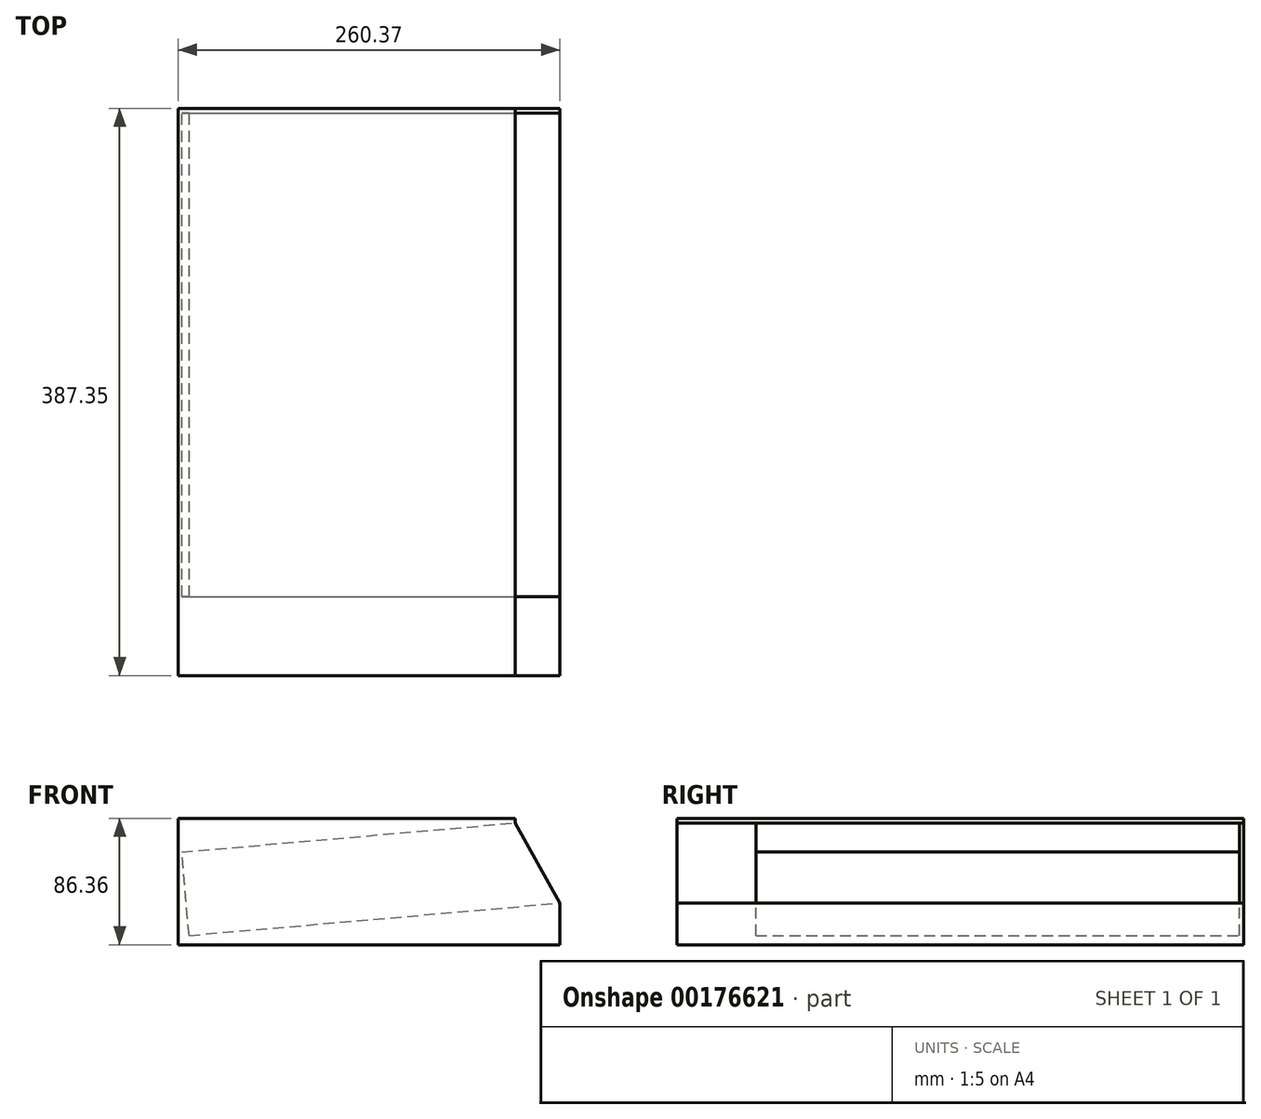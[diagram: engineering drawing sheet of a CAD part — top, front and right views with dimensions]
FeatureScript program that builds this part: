
annotation { "Feature Type Name" : "Feature", "Feature Type Description" : "" }
export const myFeature = defineFeature(function(context is Context, id is Id, definition is map)
    precondition{}
    {
        {
            var Q0;
            Q0=qCreatedBy(makeId("Front.planeOp"),FACE);
            var sketch = newSketch(context, id + "F0", { "sketchPlane" : qUnion([Q0])});
            skLineSegment(sketch, "E0", {"start": v(-29.65, 0) * mm, "end": v(230.72, 0) * mm});
            skLineSegment(sketch, "E1", {"start": v(-29.65, 0) * mm, "end": v(-29.65, 86.36) * mm});
            skLineSegment(sketch, "E2", {"start": v(-22.32, 6.35) * mm, "end": v(-27.3, 63.28) * mm});
            skLineSegment(sketch, "E3", {"start": v(-22.32, 6.35) * mm, "end": v(230.72, 28.49) * mm});
            skLineSegment(sketch, "E4", {"start": v(-27.3, 63.28) * mm, "end": v(200.43, 83.2) * mm});
            skLineSegment(sketch, "E5", {"start": v(-29.65, 86.36) * mm, "end": v(200.43, 86.36) * mm});
            skLineSegment(sketch, "E6", {"start": v(230.72, 28.49) * mm, "end": v(230.72, 0) * mm});
            skLineSegment(sketch, "E7", {"start": v(200.43, 83.2) * mm, "end": v(200.43, 86.36) * mm});
            skLineSegment(sketch, "E8", {"start": v(200.43, 83.2) * mm, "end": v(230.72, 28.49) * mm});
            skSolve(sketch);
        }
        {
            var Q0;
            Q0=makeQuery(id+"F0.imprint","IMPRINT",FACE,{"disambiguationData":[TD([[makeQuery(id+"F0.imprint","IMPRINT",EDGE,{"derivedFrom":sQuery(id+"F0.wireOp",EDGE,"E0")}),1.0]])]});
            var Q1;
            Q1=makeQuery(id+"F0.imprint","IMPRINT",FACE,{"disambiguationData":[TD([[makeQuery(id+"F0.imprint","IMPRINT",EDGE,{"derivedFrom":sQuery(id+"F0.wireOp",EDGE,"E2")}),-1.0]])]});
            extrude(context, id + "F1", {"entities" : qUnion([Q0, Q1]), "oppositeDirection" : true, "depth" : 3.17 * mm});
        }
        {
            var Q0;
            Q0=makeQuery(id+"F0.imprint","IMPRINT",FACE,{"disambiguationData":[TD([[makeQuery(id+"F0.imprint","IMPRINT",EDGE,{"derivedFrom":sQuery(id+"F0.wireOp",EDGE,"E0")}),1.0]])]});
            extrude(context, id + "F2", {"entities" : qUnion([Q0]), "operationType" : NewBodyOperationType.ADD, "depth" : 330.2 * mm});
        }
        {
            var Q0;
            Q0=makeQuery(id+"F2.opExtrude","CAP_FACE",FACE,{"disambiguationData":[OSD([sQuery(id+"F0.wireOp",EDGE,"E0"),sQuery(id+"F0.wireOp",EDGE,"E1"),sQuery(id+"F0.wireOp",EDGE,"E2"),sQuery(id+"F0.wireOp",EDGE,"E3"),sQuery(id+"F0.wireOp",EDGE,"E4"),sQuery(id+"F0.wireOp",EDGE,"E5"),sQuery(id+"F0.wireOp",EDGE,"E6"),sQuery(id+"F0.wireOp",EDGE,"E7")])],"isStart":false});
            var sketch = newSketch(context, id + "F3", { "sketchPlane" : qUnion([Q0])});
            skLineSegment(sketch, "E9", {"start": v(200.43, 83.2) * mm, "end": v(230.72, 28.49) * mm});
            skLineSegment(sketch, "E10", {"start": v(230.72, 28.49) * mm, "end": v(230.72, 0) * mm});
            skLineSegment(sketch, "E11", {"start": v(230.72, 0) * mm, "end": v(-29.65, 0) * mm});
            skLineSegment(sketch, "E12", {"start": v(-29.65, 0) * mm, "end": v(-29.65, 86.36) * mm});
            skLineSegment(sketch, "E13", {"start": v(-29.65, 86.36) * mm, "end": v(200.43, 86.36) * mm});
            skLineSegment(sketch, "E14", {"start": v(200.43, 86.36) * mm, "end": v(200.43, 83.2) * mm});
            skLineSegment(sketch, "E15", {"start": v(200.43, 83.2) * mm, "end": v(-27.3, 63.28) * mm});
            skLineSegment(sketch, "E16", {"start": v(-27.3, 63.28) * mm, "end": v(-22.32, 6.35) * mm});
            skLineSegment(sketch, "E17", {"start": v(-22.32, 6.35) * mm, "end": v(230.72, 28.49) * mm});
            skSolve(sketch);
        }
        {
            var Q0;
            Q0=makeQuery(id+"F3.imprint","IMPRINT",FACE,{"disambiguationData":[TD([[makeQuery(id+"F3.imprint","IMPRINT",EDGE,{"derivedFrom":sQuery(id+"F3.wireOp",EDGE,"E10")}),-1.0]])]});
            var Q1;
            Q1=makeQuery(id+"F3.imprint","IMPRINT",FACE,{"disambiguationData":[TD([[makeQuery(id+"F3.imprint","IMPRINT",EDGE,{"derivedFrom":sQuery(id+"F3.wireOp",EDGE,"E9")}),-1.0]])]});
            extrude(context, id + "F4", {"entities" : qUnion([Q0, Q1]), "operationType" : NewBodyOperationType.ADD, "depth" : 53.97 * mm});
        }
    });
